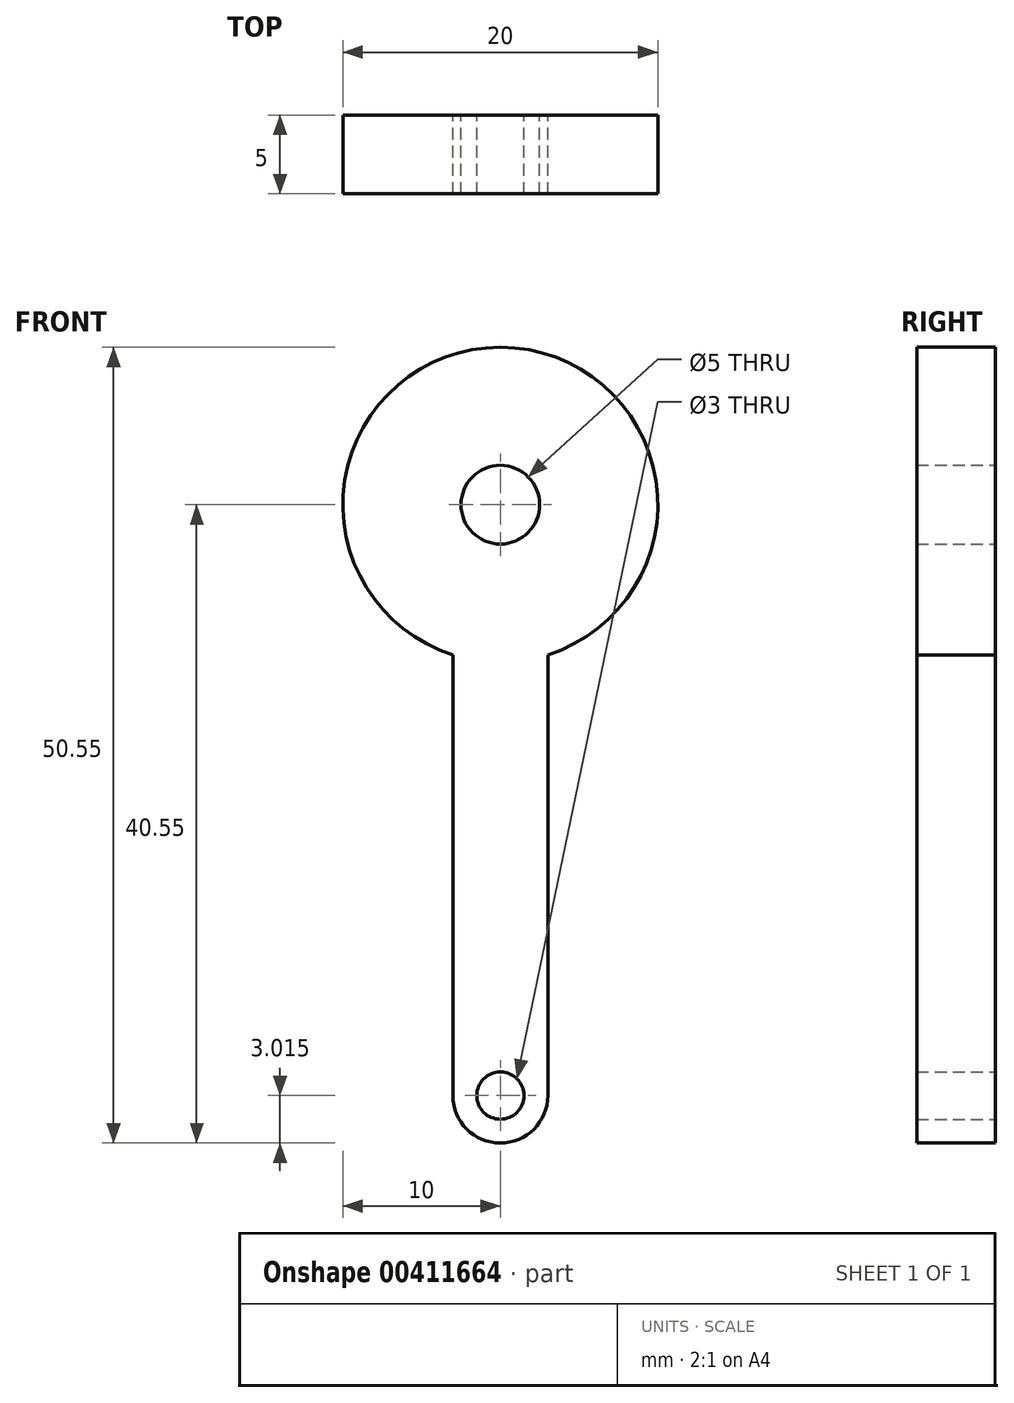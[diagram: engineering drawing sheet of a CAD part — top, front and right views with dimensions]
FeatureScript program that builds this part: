
annotation { "Feature Type Name" : "Feature", "Feature Type Description" : "" }
export const myFeature = defineFeature(function(context is Context, id is Id, definition is map)
    precondition{}
    {
        {
            var Q0;
            Q0=qCreatedBy(makeId("Front.planeOp"),FACE);
            var sketch = newSketch(context, id + "F0", { "sketchPlane" : qUnion([Q0])});
            skArc(sketch, "E0", {"start": v(3.01, -9.53) * mm, "mid": v(0, 10) * mm, "end": v(-3.01, -9.53) * mm});
            skLineSegment(sketch, "E1", {"start": v(3.01, -9.53) * mm, "end": v(3.01, -37.53) * mm});
            skLineSegment(sketch, "E2", {"start": v(-3.01, -9.53) * mm, "end": v(-3.01, -37.53) * mm});
            skLineSegment(sketch, "E3", {"start": v(0, 21.57) * mm, "end": v(0, -61.5) * mm, "construction": true});
            skLineSegment(sketch, "E4", {"start": v(-3.01, -37.53) * mm, "end": v(3.01, -37.53) * mm, "construction": true});
            skPoint(sketch, "E5.center.orphan", {"position": v(0, -37.53) * mm});
            skArc(sketch, "E6", {"start": v(-3.01, -37.53) * mm, "mid": v(0, -40.55) * mm, "end": v(3.01, -37.53) * mm});
            skCircle(sketch, "E7", {"center": v(0, 0) * mm, "radius": 2.5 * mm});
            skCircle(sketch, "E8", {"center": v(0, -37.53) * mm, "radius": 1.5 * mm});
            skSolve(sketch);
        }
        {
            var Q0;
            Q0 = qSketchRegion(id + "F0", true);
            extrude(context, id + "F1", {"entities" : qUnion([Q0]), "depth" : 5 * mm});
        }
    });
